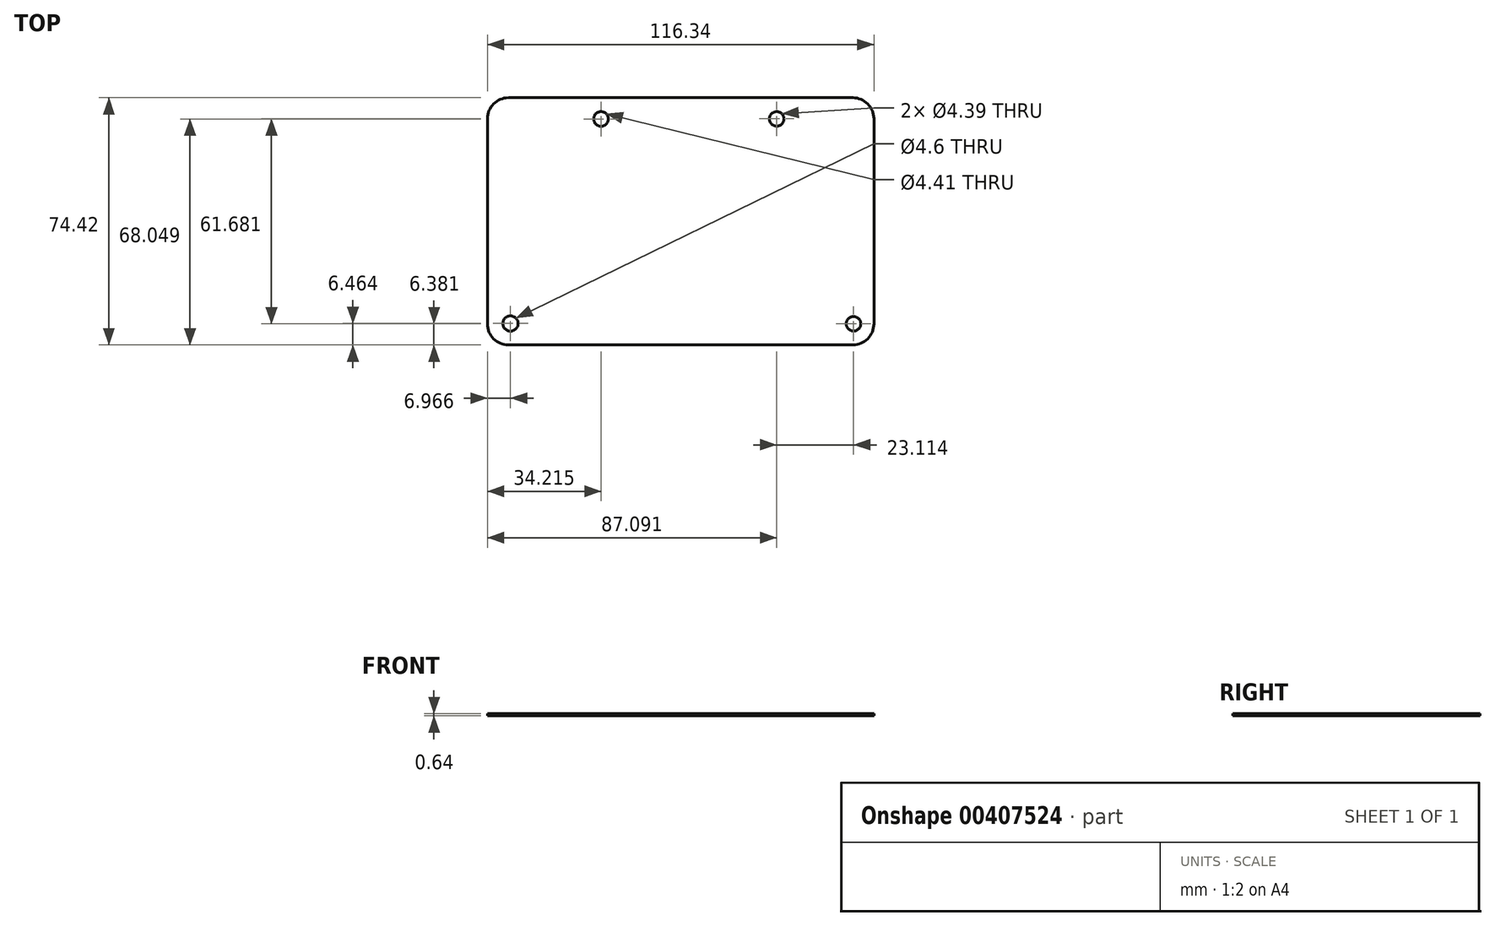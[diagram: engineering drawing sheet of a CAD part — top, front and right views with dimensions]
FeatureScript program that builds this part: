
annotation { "Feature Type Name" : "Feature", "Feature Type Description" : "" }
export const myFeature = defineFeature(function(context is Context, id is Id, definition is map)
    precondition{}
    {
        {
            var Q0;
            Q0=qCreatedBy(makeId("Top.planeOp"),FACE);
            var sketch = newSketch(context, id + "F0", { "sketchPlane" : qUnion([Q0])});
            skLineSegment(sketch, "E0.bottom", {"start": v(-51.82, 37.21) * mm, "end": v(51.82, 37.21) * mm});
            skLineSegment(sketch, "E0.top", {"start": v(-51.82, -37.21) * mm, "end": v(51.82, -37.21) * mm});
            skLineSegment(sketch, "E0.left", {"start": v(-58.17, 30.86) * mm, "end": v(-58.17, -30.86) * mm});
            skLineSegment(sketch, "E0.right", {"start": v(58.17, 30.86) * mm, "end": v(58.17, -30.86) * mm});
            skPoint(sketch, "E0.middle", {"position": v(0, 0) * mm});
            skPoint(sketch, "E1.visualSharp", {"position": v(-58.17, 37.21) * mm});
            skArc(sketch, "E1.filletArc", {"start": v(-51.82, 37.21) * mm, "mid": v(-56.3, 35.35) * mm, "end": v(-58.17, 30.86) * mm});
            skPoint(sketch, "E2.visualSharp", {"position": v(58.17, 37.21) * mm});
            skArc(sketch, "E2.filletArc", {"start": v(58.17, 30.86) * mm, "mid": v(56.3, 35.35) * mm, "end": v(51.82, 37.21) * mm});
            skPoint(sketch, "E3.visualSharp", {"position": v(-58.17, -37.21) * mm});
            skArc(sketch, "E3.filletArc", {"start": v(-58.17, -30.86) * mm, "mid": v(-56.3, -35.35) * mm, "end": v(-51.82, -37.21) * mm});
            skPoint(sketch, "E4.visualSharp", {"position": v(58.17, -37.21) * mm});
            skArc(sketch, "E4.filletArc", {"start": v(51.82, -37.21) * mm, "mid": v(56.3, -35.35) * mm, "end": v(58.17, -30.86) * mm});
            skCircle(sketch, "E5", {"center": v(-51.2, -30.75) * mm, "radius": 2.3 * mm});
            skCircle(sketch, "E6", {"center": v(52.03, -30.83) * mm, "radius": 2.2 * mm});
            skCircle(sketch, "E7", {"center": v(-23.96, 30.84) * mm, "radius": 2.2 * mm});
            skCircle(sketch, "E8", {"center": v(28.92, 30.85) * mm, "radius": 2.2 * mm});
            skSolve(sketch);
        }
        {
            var Q0;
            Q0 = qSketchRegion(id + "F0", true);
            extrude(context, id + "F1", {"entities" : qUnion([Q0]), "depth" : 0.64 * mm});
        }
    });
